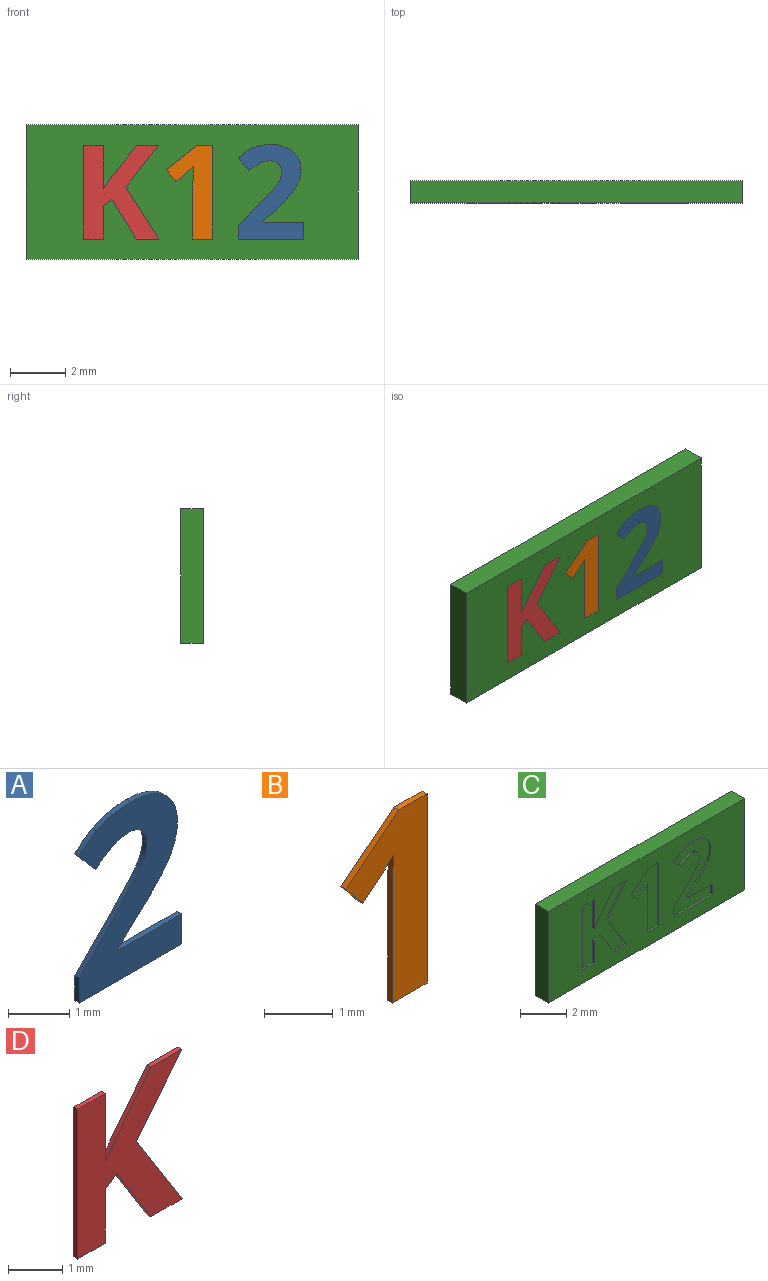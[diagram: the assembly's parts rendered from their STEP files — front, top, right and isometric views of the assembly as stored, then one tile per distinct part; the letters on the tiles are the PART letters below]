
ASSEMBLY  parts=4 mates=3
PART A: 26 faces, bbox 2.4x0.1x3.4 mm
  f0: plane 3.42x2.37mm, normal (0,-1,0), area 4.2mm2, adj f1,f2,f3,f4,f5,f6,f7,f8
  f1: plane 1.47x0.1mm, normal (0,0,1), area 0.1mm2, adj f0,f2,f22,f24
  f2: plane 0.1x0.03mm, normal (1,0,0), area 0mm2, adj f0,f1,f3,f22
  f3: plane 0.43x0.41mm, normal (0.69,0,-0.73), area 0.1mm2, adj f0,f2,f4,f22
  f4: extruded ~0.61x0.61mm, area 0.1mm2, adj f0,f3,f5,f22
  f5: extruded ~0.42x0.25mm, area 0mm2, adj f0,f4,f6,f22
  f6: extruded ~0.44x0.1mm, area 0mm2, adj f0,f5,f7,f22
  f7: extruded ~0.48x0.13mm, area 0.1mm2, adj f0,f6,f8,f22
  f8: extruded ~0.38x0.32mm, area 0.1mm2, adj f0,f7,f9,f22
  f9: extruded ~0.56x0.12mm, area 0.1mm2, adj f0,f8,f10,f22
  f10: extruded ~0.43x0.1mm, area 0mm2, adj f0,f9,f11,f22
  f11: extruded ~0.36x0.13mm, area 0mm2, adj f0,f10,f12,f22
  f12: extruded ~0.41x0.3mm, area 0.1mm2, adj f0,f11,f13,f22
  f13: plane 0.46x0.39mm, normal (-0.76,0,-0.65), area 0.1mm2, adj f0,f12,f14,f22
  f14: extruded ~0.39x0.26mm, area 0mm2, adj f0,f13,f15,f22
  f15: extruded ~0.38x0.1mm, area 0mm2, adj f0,f14,f16,f22
  f16: extruded ~0.3x0.1mm, area 0mm2, adj f0,f15,f17,f22
  f17: extruded ~0.3x0.11mm, area 0mm2, adj f0,f16,f18,f22
  f18: extruded ~0.26x0.1mm, area 0mm2, adj f0,f17,f19,f22
  f19: extruded ~0.28x0.17mm, area 0mm2, adj f0,f18,f20,f22
  f20: extruded ~0.53x0.49mm, area 0.1mm2, adj f0,f19,f21,f22
  f21: plane 0.86x0.85mm, normal (-0.71,0,0.7), area 0.1mm2, adj f0,f20,f22,f23
  f22: plane 3.42x2.37mm, normal (0,1,0), area 4.2mm2, adj f1,f2,f3,f4,f5,f6,f7,f8
  f23: plane 0.5x0.1mm, normal (-1,0,0), area 0mm2, adj f0,f21,f22,f25
  f24: plane 0.6x0.1mm, normal (1,0,0), area 0.1mm2, adj f0,f1,f22,f25
  f25: plane 2.36x0.1mm, normal (0,0,-1), area 0.2mm2, adj f0,f22,f23,f24
PART B: 12 faces, bbox 1.7x0.1x3.4 mm
  f0: plane 3.37x1.67mm, normal (0,-1,0), area 2.9mm2, adj f1,f2,f3,f4,f5,f6,f7,f9
  f1: plane 0.59x0.1mm, normal (0,0,1), area 0.1mm2, adj f0,f2,f8,f10
  f2: plane 1.09x0.86mm, normal (-0.62,0,0.78), area 0.1mm2, adj f0,f1,f3,f8
  f3: plane 0.43x0.34mm, normal (-0.78,0,-0.63), area 0.1mm2, adj f0,f2,f4,f8
  f4: plane 0.39x0.31mm, normal (0.63,0,-0.78), area 0mm2, adj f0,f3,f5,f8
  f5: extruded ~0.25x0.23mm, area 0mm2, adj f0,f4,f6,f8
  f6: plane 0.35x0.1mm, normal (-1,0,0.03), area 0mm2, adj f0,f5,f7,f8
  f7: plane 0.32x0.1mm, normal (-1,0,0.02), area 0mm2, adj f0,f6,f8,f9
  f8: plane 3.37x1.67mm, normal (0,1,0), area 2.9mm2, adj f1,f2,f3,f4,f5,f6,f7,f9
  f9: plane 1.95x0.1mm, normal (-1,0,0), area 0.2mm2, adj f0,f7,f8,f11
  f10: plane 3.37x0.1mm, normal (1,0,0), area 0.3mm2, adj f0,f1,f8,f11
  f11: plane 0.71x0.1mm, normal (0,0,-1), area 0.1mm2, adj f0,f8,f9,f10
PART C: 56 faces, bbox 12x0.8x4.9 mm
  f0: plane 12x4.85mm, normal (0,-1,0), area 45.8mm2, adj f1,f2,f3,f4,f6,f7,f8,f9
  f1: plane 12x0.8mm, normal (0,0,-1), area 9.6mm2, adj f0,f2,f4,f5
  f2: plane 4.85x0.8mm, normal (1,0,0), area 3.9mm2, adj f0,f1,f3,f5
  f3: plane 12x0.8mm, normal (0,0,1), area 9.6mm2, adj f0,f2,f4,f5
  f4: plane 4.85x0.8mm, normal (-1,0,0), area 3.9mm2, adj f0,f1,f3,f5
  f5: plane 12x4.85mm, normal (0,1,0), area 58.2mm2, adj f1,f2,f3,f4
  f6: plane 0.6x0.1mm, normal (-1,0,0), area 0.1mm2, adj f0,f7,f29,f30
  f7: plane 1.47x0.1mm, normal (0,0,-1), area 0.1mm2, adj f0,f6,f8,f30
  f8: plane 0.1x0.03mm, normal (-1,0,0), area 0mm2, adj f0,f7,f9,f30
  f9: plane 0.43x0.41mm, normal (-0.69,0,0.73), area 0.1mm2, adj f0,f8,f10,f30
  f10: extruded ~0.61x0.61mm, area 0.1mm2, adj f0,f9,f11,f30
  f11: extruded ~0.42x0.25mm, area 0mm2, adj f0,f10,f12,f30
  f12: extruded ~0.44x0.1mm, area 0mm2, adj f0,f11,f13,f30
  f13: extruded ~0.48x0.13mm, area 0.1mm2, adj f0,f12,f14,f30
  f14: extruded ~0.38x0.32mm, area 0.1mm2, adj f0,f13,f15,f30
  f15: extruded ~0.56x0.12mm, area 0.1mm2, adj f0,f14,f16,f30
  f16: extruded ~0.43x0.1mm, area 0mm2, adj f0,f15,f17,f30
  f17: extruded ~0.36x0.13mm, area 0mm2, adj f0,f16,f18,f30
  f18: extruded ~0.41x0.3mm, area 0.1mm2, adj f0,f17,f19,f30
  f19: plane 0.46x0.39mm, normal (0.76,0,0.65), area 0.1mm2, adj f0,f18,f20,f30
  f20: extruded ~0.39x0.26mm, area 0mm2, adj f0,f19,f21,f30
  f21: extruded ~0.38x0.1mm, area 0mm2, adj f0,f20,f22,f30
  f22: extruded ~0.3x0.1mm, area 0mm2, adj f0,f21,f23,f30
  f23: extruded ~0.3x0.11mm, area 0mm2, adj f0,f22,f24,f30
  f24: extruded ~0.26x0.1mm, area 0mm2, adj f0,f23,f25,f30
  f25: extruded ~0.28x0.17mm, area 0mm2, adj f0,f24,f26,f30
  f26: extruded ~0.53x0.49mm, area 0.1mm2, adj f0,f25,f27,f30
  f27: plane 0.86x0.85mm, normal (0.71,0,-0.7), area 0.1mm2, adj f0,f26,f28,f30
  f28: plane 0.5x0.1mm, normal (1,0,0), area 0mm2, adj f0,f27,f29,f30
  f29: plane 2.36x0.1mm, normal (0,0,1), area 0.2mm2, adj f0,f6,f28,f30
  f30: plane 3.42x2.37mm, normal (0,-1,0), area 4.2mm2, adj f6,f7,f8,f9,f10,f11,f12,f13
  f31: plane 3.37x0.1mm, normal (-1,0,0), area 0.3mm2, adj f0,f32,f40,f41
  f32: plane 0.59x0.1mm, normal (0,0,-1), area 0.1mm2, adj f0,f31,f33,f41
  f33: plane 1.09x0.86mm, normal (0.62,0,-0.78), area 0.1mm2, adj f0,f32,f34,f41
  f34: plane 0.43x0.34mm, normal (0.78,0,0.63), area 0.1mm2, adj f0,f33,f35,f41
  f35: plane 0.39x0.31mm, normal (-0.63,0,0.78), area 0mm2, adj f0,f34,f36,f41
  f36: extruded ~0.25x0.23mm, area 0mm2, adj f0,f35,f37,f41
  f37: plane 0.35x0.1mm, normal (1,0,-0.03), area 0mm2, adj f0,f36,f38,f41
  f38: plane 0.32x0.1mm, normal (1,0,-0.02), area 0mm2, adj f0,f37,f39,f41
  f39: plane 1.95x0.1mm, normal (1,0,0), area 0.2mm2, adj f0,f38,f40,f41
  f40: plane 0.71x0.1mm, normal (0,0,1), area 0.1mm2, adj f0,f31,f39,f41
  f41: plane 3.37x1.67mm, normal (0,-1,0), area 2.9mm2, adj f31,f32,f33,f34,f35,f36,f37,f38
  f42: plane 1.88x1.19mm, normal (-0.85,0,-0.53), area 0.2mm2, adj f0,f43,f54,f55
  f43: plane 1.49x1.18mm, normal (-0.79,0,0.62), area 0.2mm2, adj f0,f42,f44,f55
  f44: plane 0.79x0.1mm, normal (0,0,-1), area 0.1mm2, adj f0,f43,f45,f55
  f45: plane 1.15x0.91mm, normal (0.78,0,-0.62), area 0.1mm2, adj f0,f44,f46,f55
  f46: plane 0.4x0.28mm, normal (0.82,0,-0.58), area 0mm2, adj f0,f45,f47,f55
  f47: plane 1.54x0.1mm, normal (-1,0,0), area 0.2mm2, adj f0,f46,f48,f55
  f48: plane 0.72x0.1mm, normal (0,0,-1), area 0.1mm2, adj f0,f47,f49,f55
  f49: plane 3.37x0.1mm, normal (1,0,0), area 0.3mm2, adj f0,f48,f50,f55
  f50: plane 0.72x0.1mm, normal (0,0,1), area 0.1mm2, adj f0,f49,f51,f55
  f51: plane 1.2x0.1mm, normal (-1,0,0), area 0.1mm2, adj f0,f50,f52,f55
  f52: plane 0.3x0.22mm, normal (-0.58,0,0.81), area 0mm2, adj f0,f51,f53,f55
  f53: plane 1.42x0.88mm, normal (0.85,0,0.53), area 0.2mm2, adj f0,f52,f54,f55
  f54: plane 0.81x0.1mm, normal (0,0,1), area 0.1mm2, adj f0,f42,f53,f55
  f55: plane 3.37x2.71mm, normal (0,-1,0), area 5.2mm2, adj f42,f43,f44,f45,f46,f47,f48,f49
PART D: 15 faces, bbox 2.7x0.1x3.4 mm
  f0: plane 3.37x2.71mm, normal (0,-1,0), area 5.2mm2, adj f1,f2,f3,f4,f5,f6,f7,f8
  f1: plane 1.49x1.18mm, normal (0.79,0,-0.62), area 0.2mm2, adj f0,f2,f11,f13
  f2: plane 0.79x0.1mm, normal (0,0,1), area 0.1mm2, adj f0,f1,f3,f11
  f3: plane 1.15x0.91mm, normal (-0.78,0,0.62), area 0.1mm2, adj f0,f2,f4,f11
  f4: plane 0.4x0.28mm, normal (-0.82,0,0.58), area 0mm2, adj f0,f3,f5,f11
  f5: plane 1.54x0.1mm, normal (1,0,0), area 0.2mm2, adj f0,f4,f6,f11
  f6: plane 0.72x0.1mm, normal (0,0,1), area 0.1mm2, adj f0,f5,f7,f11
  f7: plane 3.37x0.1mm, normal (-1,0,0), area 0.3mm2, adj f0,f6,f8,f11
  f8: plane 0.72x0.1mm, normal (0,0,-1), area 0.1mm2, adj f0,f7,f9,f11
  f9: plane 1.2x0.1mm, normal (1,0,0), area 0.1mm2, adj f0,f8,f10,f11
  f10: plane 0.3x0.22mm, normal (0.58,0,-0.81), area 0mm2, adj f0,f9,f11,f12
  f11: plane 3.37x2.71mm, normal (0,1,0), area 5.2mm2, adj f1,f2,f3,f4,f5,f6,f7,f8
  f12: plane 1.42x0.88mm, normal (-0.85,0,-0.53), area 0.2mm2, adj f0,f10,f11,f14
  f13: plane 1.88x1.19mm, normal (0.85,0,0.53), area 0.2mm2, adj f0,f1,f11,f14
  f14: plane 0.81x0.1mm, normal (0,0,-1), area 0.1mm2, adj f0,f11,f12,f13
PLACE A t=(1.35,0.4,0.01)mm
PLACE B t=(-1.64,0.4,0.01)mm
PLACE C t=(0.01,0.4,0.01)mm
PLACE D t=(-1.64,0.4,0.01)mm
MATE fastened A.f0 <-> C.f0  axis (0,-1,0) through (1.69,-0.4,-1.69)mm
MATE fastened D.f0 <-> C.f0  axis (0,-1,0) through (-3.91,-0.4,-1.69)mm
MATE fastened B.f0 <-> C.f0  axis (0,-1,0) through (0.04,-0.4,-1.69)mm
